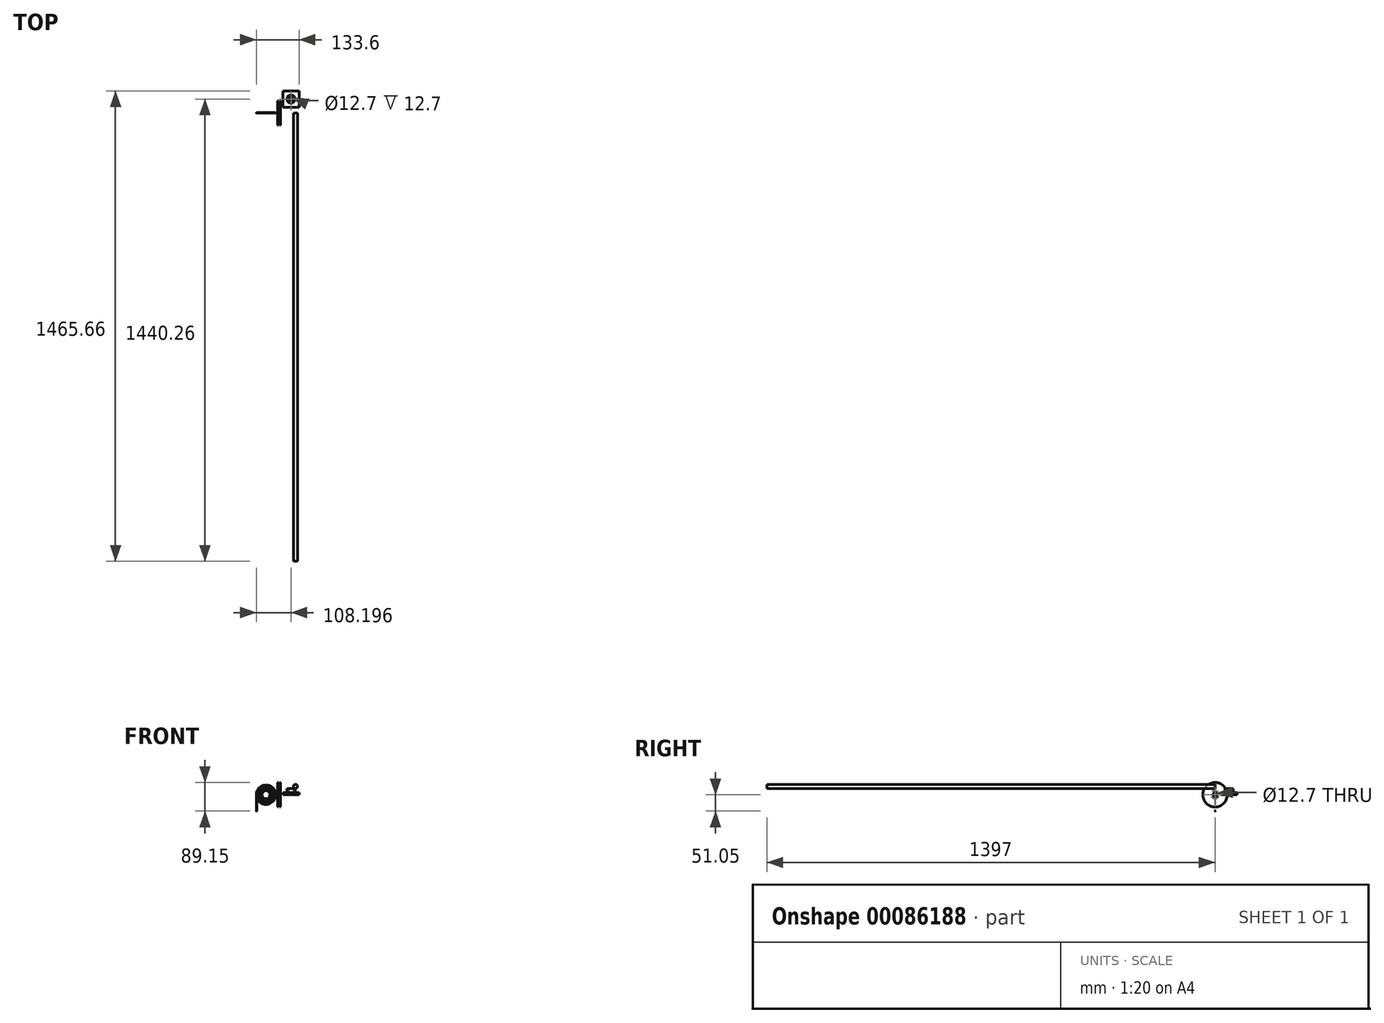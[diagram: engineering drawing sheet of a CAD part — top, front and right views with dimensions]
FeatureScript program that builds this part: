
annotation { "Feature Type Name" : "Feature", "Feature Type Description" : "" }
export const myFeature = defineFeature(function(context is Context, id is Id, definition is map)
    precondition{}
    {
        {
            var Q0;
            Q0=qCreatedBy(makeId("Front.planeOp"),FACE);
            var sketch = newSketch(context, id + "F0", { "sketchPlane" : qUnion([Q0])});
            skLineSegment(sketch, "E0", {"start": v(0, 0) * mm, "end": v(-68.9, 0) * mm, "construction": true});
            skLineSegment(sketch, "E1", {"start": v(0, 0) * mm, "end": v(0, 60.17) * mm, "construction": true});
            skLineSegment(sketch, "E2", {"start": v(-4.76, 6.35) * mm, "end": v(-4.76, 38.1) * mm});
            skLineSegment(sketch, "E3", {"start": v(-4.76, 38.1) * mm, "end": v(-1.59, 38.1) * mm});
            skLineSegment(sketch, "E4", {"start": v(-1.59, 38.1) * mm, "end": v(-1.59, 12.7) * mm});
            skLineSegment(sketch, "E5", {"start": v(-1.59, 12.7) * mm, "end": v(0, 12.7) * mm});
            skLineSegment(sketch, "E6", {"start": v(0, 12.7) * mm, "end": v(0, 6.35) * mm});
            skLineSegment(sketch, "E7", {"start": v(0, 6.35) * mm, "end": v(-4.76, 6.35) * mm});
            skLineSegment(sketch, "E8.MirrorCS", {"start": v(1.59, 12.7) * mm, "end": v(0, 12.7) * mm});
            skLineSegment(sketch, "E9.MirrorCS", {"start": v(1.59, 38.1) * mm, "end": v(1.59, 12.7) * mm});
            skLineSegment(sketch, "E10.MirrorCS", {"start": v(4.76, 38.1) * mm, "end": v(1.59, 38.1) * mm});
            skLineSegment(sketch, "E11.MirrorCS", {"start": v(4.76, 6.35) * mm, "end": v(4.76, 38.1) * mm});
            skLineSegment(sketch, "E12.MirrorCS", {"start": v(0, 6.35) * mm, "end": v(4.76, 6.35) * mm});
            skSolve(sketch);
        }
        {
            var Q0;
            Q0=makeQuery(id+"F0.imprint","IMPRINT",FACE,{"disambiguationData":[TD([[makeQuery(id+"F0.imprint","IMPRINT",EDGE,{"derivedFrom":sQuery(id+"F0.wireOp",EDGE,"E2")}),-1.0]])]});
            var Q1;
            Q1=makeQuery(id+"F0.imprint","IMPRINT",FACE,{"disambiguationData":[TD([[makeQuery(id+"F0.imprint","IMPRINT",EDGE,{"derivedFrom":sQuery(id+"F0.wireOp",EDGE,"E6")}),1.0]])]});
            var Q2;
            Q2=sQuery(id+"F0.wireOp",EDGE,"E0");
            revolve(context, id + "F1", {"entities" : qUnion([Q0, Q1]), "axis" : qUnion([Q2]), "revolveType" : RevolveType.FULL});
        }
        {
            var Q0;
            Q0=qCreatedBy(makeId("Front.planeOp"),FACE);
            var sketch = newSketch(context, id + "F2", { "sketchPlane" : qUnion([Q0])});
            skCircle(sketch, "E13", {"center": v(-40.88, 0) * mm, "radius": 12.7 * mm});
            skCircle(sketch, "E14", {"center": v(-40.88, 0) * mm, "radius": 14.29 * mm});
            skCircle(sketch, "E15", {"center": v(-40.88, 0) * mm, "radius": 15.88 * mm});
            skCircle(sketch, "E16", {"center": v(-40.88, 0) * mm, "radius": 17.46 * mm});
            skCircle(sketch, "E17", {"center": v(-40.88, 0) * mm, "radius": 19.05 * mm});
            skCircle(sketch, "E18", {"center": v(-40.88, 0) * mm, "radius": 20.64 * mm});
            skCircle(sketch, "E19", {"center": v(-40.88, 0) * mm, "radius": 22.22 * mm});
            skCircle(sketch, "E20", {"center": v(-40.88, 0) * mm, "radius": 23.81 * mm});
            skCircle(sketch, "E21", {"center": v(-40.88, 0) * mm, "radius": 25.4 * mm});
            skCircle(sketch, "E22", {"center": v(-40.88, 0) * mm, "radius": 26.99 * mm});
            skCircle(sketch, "E23", {"center": v(-40.88, 0) * mm, "radius": 28.57 * mm});
            skArc(sketch, "E24", {"start": v(-69.45, -9.66) * mm, "mid": v(-11.12, 4.9) * mm, "end": v(-71.04, 0) * mm});
            skLineSegment(sketch, "E25", {"start": v(-71.04, 0) * mm, "end": v(-71.04, -51.05) * mm});
            skLineSegment(sketch, "E26", {"start": v(-69.45, 0) * mm, "end": v(-69.45, -51.05) * mm});
            skLineSegment(sketch, "E27", {"start": v(-71.04, -51.05) * mm, "end": v(-69.45, -51.05) * mm});
            skSolve(sketch);
        }
        {
            var Q0;
            Q0=qCreatedBy(makeId("Top.planeOp"),FACE);
            var sketch = newSketch(context, id + "F3", { "sketchPlane" : qUnion([Q0])});
            skLineSegment(sketch, "E28.0", {"start": v(-10.72, 0) * mm, "end": v(-71.04, 0) * mm});
            skLineSegment(sketch, "E28.1", {"start": v(-12.3, 0) * mm, "end": v(-69.45, 0) * mm});
            skLineSegment(sketch, "E28.2", {"start": v(-13.9, 0) * mm, "end": v(-67.87, 0) * mm});
            skLineSegment(sketch, "E28.3", {"start": v(-15.48, 0) * mm, "end": v(-66.28, 0) * mm});
            skLineSegment(sketch, "E28.4", {"start": v(-17.07, 0) * mm, "end": v(-64.7, 0) * mm});
            skLineSegment(sketch, "E28.5", {"start": v(-18.65, 0) * mm, "end": v(-63.1, 0) * mm});
            skLineSegment(sketch, "E28.6", {"start": v(-20.24, 0) * mm, "end": v(-61.52, 0) * mm});
            skLineSegment(sketch, "E28.7", {"start": v(-21.83, 0) * mm, "end": v(-59.93, 0) * mm});
            skLineSegment(sketch, "E28.8", {"start": v(-23.42, 0) * mm, "end": v(-58.34, 0) * mm});
            skLineSegment(sketch, "E28.9", {"start": v(-25, 0) * mm, "end": v(-56.75, 0) * mm});
            skLineSegment(sketch, "E28.10", {"start": v(-26.6, 0) * mm, "end": v(-55.17, 0) * mm});
            skLineSegment(sketch, "E28.11", {"start": v(-28.18, 0) * mm, "end": v(-53.58, 0) * mm});
            skLineSegment(sketch, "E28.14", {"start": v(-71.04, 0) * mm, "end": v(-69.45, 0) * mm});
            skCircle(sketch, "E29", {"center": v(-11.5, 0) * mm, "radius": 0.8 * mm});
            skCircle(sketch, "E30", {"center": v(-13.1, 0) * mm, "radius": 0.8 * mm});
            skCircle(sketch, "E31", {"center": v(-14.68, 0) * mm, "radius": 0.8 * mm});
            skCircle(sketch, "E32", {"center": v(-16.27, 0) * mm, "radius": 0.8 * mm});
            skCircle(sketch, "E33", {"center": v(-17.86, 0) * mm, "radius": 0.8 * mm});
            skCircle(sketch, "E34", {"center": v(-19.45, 0) * mm, "radius": 0.8 * mm});
            skCircle(sketch, "E35", {"center": v(-21.03, 0) * mm, "radius": 0.8 * mm});
            skCircle(sketch, "E36", {"center": v(-22.62, 0) * mm, "radius": 0.8 * mm});
            skCircle(sketch, "E37", {"center": v(-24.2, 0) * mm, "radius": 0.8 * mm});
            skCircle(sketch, "E38", {"center": v(-25.8, 0) * mm, "radius": 0.8 * mm});
            skCircle(sketch, "E39", {"center": v(-27.38, 0) * mm, "radius": 0.8 * mm});
            skSolve(sketch);
        }
        {
            var Q0;
            {var subQ0=sQuery(id+"F3.wireOp",EDGE,"E28.0");Q0=makeQuery(id+"F3.imprint","IMPRINT",FACE,{"disambiguationData":[TD([[makeQuery(id+"F3.imprint","IMPRINT",EDGE,{"derivedFrom":subQ0}),-1.0]])]});}
            var Q1;
            {var subQ0=sQuery(id+"F3.wireOp",EDGE,"E30");var subQ1=sQuery(id+"F3.wireOp",EDGE,"E28.1");var subQ2=makeQuery(id+"F3.imprint","INTERSECT",VERTEX,{"derivedFrom":[sQuery(id+"F3.wireOp",EDGE,"E28.0"),subQ1,sQuery(id+"F3.wireOp",EDGE,"E29"),subQ0]});Q1=makeQuery(id+"F3.imprint","IMPRINT",FACE,{"disambiguationData":[TD([[makeQuery(id+"F3.imprint","IMPRINT",EDGE,{"disambiguationData":[TD([[subQ2,-1.0]])],"derivedFrom":subQ1}),-1.0]])]});}
            var Q2;
            {var subQ0=sQuery(id+"F3.wireOp",EDGE,"E31");var subQ1=sQuery(id+"F3.wireOp",EDGE,"E28.2");var subQ2=makeQuery(id+"F3.imprint","INTERSECT",VERTEX,{"derivedFrom":[sQuery(id+"F3.wireOp",EDGE,"E28.1"),subQ1,sQuery(id+"F3.wireOp",EDGE,"E30"),subQ0]});Q2=makeQuery(id+"F3.imprint","IMPRINT",FACE,{"disambiguationData":[TD([[makeQuery(id+"F3.imprint","IMPRINT",EDGE,{"disambiguationData":[TD([[subQ2,-1.0]])],"derivedFrom":subQ1}),-1.0]])]});}
            var Q3;
            {var subQ0=sQuery(id+"F3.wireOp",EDGE,"E32");var subQ1=sQuery(id+"F3.wireOp",EDGE,"E28.3");var subQ2=makeQuery(id+"F3.imprint","INTERSECT",VERTEX,{"derivedFrom":[sQuery(id+"F3.wireOp",EDGE,"E28.2"),subQ1,sQuery(id+"F3.wireOp",EDGE,"E31"),subQ0]});Q3=makeQuery(id+"F3.imprint","IMPRINT",FACE,{"disambiguationData":[TD([[makeQuery(id+"F3.imprint","IMPRINT",EDGE,{"disambiguationData":[TD([[subQ2,-1.0]])],"derivedFrom":subQ1}),-1.0]])]});}
            var Q4;
            {var subQ0=sQuery(id+"F3.wireOp",EDGE,"E33");var subQ1=sQuery(id+"F3.wireOp",EDGE,"E28.4");var subQ2=makeQuery(id+"F3.imprint","INTERSECT",VERTEX,{"derivedFrom":[sQuery(id+"F3.wireOp",EDGE,"E28.3"),subQ1,sQuery(id+"F3.wireOp",EDGE,"E32"),subQ0]});Q4=makeQuery(id+"F3.imprint","IMPRINT",FACE,{"disambiguationData":[TD([[makeQuery(id+"F3.imprint","IMPRINT",EDGE,{"disambiguationData":[TD([[subQ2,-1.0]])],"derivedFrom":subQ1}),-1.0]])]});}
            var Q5;
            {var subQ0=sQuery(id+"F3.wireOp",EDGE,"E34");var subQ1=sQuery(id+"F3.wireOp",EDGE,"E28.5");var subQ2=makeQuery(id+"F3.imprint","INTERSECT",VERTEX,{"derivedFrom":[sQuery(id+"F3.wireOp",EDGE,"E28.4"),subQ1,sQuery(id+"F3.wireOp",EDGE,"E33"),subQ0]});Q5=makeQuery(id+"F3.imprint","IMPRINT",FACE,{"disambiguationData":[TD([[makeQuery(id+"F3.imprint","IMPRINT",EDGE,{"disambiguationData":[TD([[subQ2,-1.0]])],"derivedFrom":subQ1}),-1.0]])]});}
            var Q6;
            {var subQ0=sQuery(id+"F3.wireOp",EDGE,"E35");var subQ1=sQuery(id+"F3.wireOp",EDGE,"E28.6");var subQ2=makeQuery(id+"F3.imprint","INTERSECT",VERTEX,{"derivedFrom":[sQuery(id+"F3.wireOp",EDGE,"E28.5"),subQ1,sQuery(id+"F3.wireOp",EDGE,"E34"),subQ0]});Q6=makeQuery(id+"F3.imprint","IMPRINT",FACE,{"disambiguationData":[TD([[makeQuery(id+"F3.imprint","IMPRINT",EDGE,{"disambiguationData":[TD([[subQ2,-1.0]])],"derivedFrom":subQ1}),-1.0]])]});}
            var Q7;
            {var subQ0=sQuery(id+"F3.wireOp",EDGE,"E36");var subQ1=sQuery(id+"F3.wireOp",EDGE,"E28.7");var subQ2=makeQuery(id+"F3.imprint","INTERSECT",VERTEX,{"derivedFrom":[sQuery(id+"F3.wireOp",EDGE,"E28.6"),subQ1,sQuery(id+"F3.wireOp",EDGE,"E35"),subQ0]});Q7=makeQuery(id+"F3.imprint","IMPRINT",FACE,{"disambiguationData":[TD([[makeQuery(id+"F3.imprint","IMPRINT",EDGE,{"disambiguationData":[TD([[subQ2,-1.0]])],"derivedFrom":subQ1}),-1.0]])]});}
            var Q8;
            {var subQ0=sQuery(id+"F3.wireOp",EDGE,"E37");var subQ1=sQuery(id+"F3.wireOp",EDGE,"E28.8");var subQ2=makeQuery(id+"F3.imprint","INTERSECT",VERTEX,{"derivedFrom":[sQuery(id+"F3.wireOp",EDGE,"E28.7"),subQ1,sQuery(id+"F3.wireOp",EDGE,"E36"),subQ0]});Q8=makeQuery(id+"F3.imprint","IMPRINT",FACE,{"disambiguationData":[TD([[makeQuery(id+"F3.imprint","IMPRINT",EDGE,{"disambiguationData":[TD([[subQ2,-1.0]])],"derivedFrom":subQ1}),-1.0]])]});}
            var Q9;
            {var subQ0=sQuery(id+"F3.wireOp",EDGE,"E38");var subQ1=sQuery(id+"F3.wireOp",EDGE,"E28.9");var subQ2=makeQuery(id+"F3.imprint","INTERSECT",VERTEX,{"derivedFrom":[sQuery(id+"F3.wireOp",EDGE,"E28.8"),subQ1,sQuery(id+"F3.wireOp",EDGE,"E37"),subQ0]});Q9=makeQuery(id+"F3.imprint","IMPRINT",FACE,{"disambiguationData":[TD([[makeQuery(id+"F3.imprint","IMPRINT",EDGE,{"disambiguationData":[TD([[subQ2,-1.0]])],"derivedFrom":subQ1}),-1.0]])]});}
            var Q10;
            {var subQ0=sQuery(id+"F3.wireOp",EDGE,"E39");var subQ1=sQuery(id+"F3.wireOp",EDGE,"E28.10");var subQ3=makeQuery(id+"F3.imprint","INTERSECT",VERTEX,{"derivedFrom":[subQ1,subQ0]});Q10=makeQuery(id+"F3.imprint","IMPRINT",FACE,{"disambiguationData":[TD([[makeQuery(id+"F3.imprint","IMPRINT",EDGE,{"disambiguationData":[TD([[subQ3,1.0]])],"derivedFrom":subQ1}),-1.0]])]});}
            var Q11;
            {var subQ0=sQuery(id+"F3.wireOp",EDGE,"E28.0");Q11=makeQuery(id+"F3.imprint","IMPRINT",FACE,{"disambiguationData":[TD([[makeQuery(id+"F3.imprint","IMPRINT",EDGE,{"derivedFrom":subQ0}),1.0]])]});}
            var Q12;
            {var subQ0=sQuery(id+"F3.wireOp",EDGE,"E30");var subQ1=sQuery(id+"F3.wireOp",EDGE,"E28.1");var subQ2=makeQuery(id+"F3.imprint","INTERSECT",VERTEX,{"derivedFrom":[sQuery(id+"F3.wireOp",EDGE,"E28.0"),subQ1,sQuery(id+"F3.wireOp",EDGE,"E29"),subQ0]});Q12=makeQuery(id+"F3.imprint","IMPRINT",FACE,{"disambiguationData":[TD([[makeQuery(id+"F3.imprint","IMPRINT",EDGE,{"disambiguationData":[TD([[subQ2,-1.0]])],"derivedFrom":subQ1}),1.0]])]});}
            var Q13;
            {var subQ0=sQuery(id+"F3.wireOp",EDGE,"E31");var subQ1=sQuery(id+"F3.wireOp",EDGE,"E28.2");var subQ2=makeQuery(id+"F3.imprint","INTERSECT",VERTEX,{"derivedFrom":[sQuery(id+"F3.wireOp",EDGE,"E28.1"),subQ1,sQuery(id+"F3.wireOp",EDGE,"E30"),subQ0]});Q13=makeQuery(id+"F3.imprint","IMPRINT",FACE,{"disambiguationData":[TD([[makeQuery(id+"F3.imprint","IMPRINT",EDGE,{"disambiguationData":[TD([[subQ2,-1.0]])],"derivedFrom":subQ1}),1.0]])]});}
            var Q14;
            {var subQ0=sQuery(id+"F3.wireOp",EDGE,"E32");var subQ1=sQuery(id+"F3.wireOp",EDGE,"E28.3");var subQ2=makeQuery(id+"F3.imprint","INTERSECT",VERTEX,{"derivedFrom":[sQuery(id+"F3.wireOp",EDGE,"E28.2"),subQ1,sQuery(id+"F3.wireOp",EDGE,"E31"),subQ0]});Q14=makeQuery(id+"F3.imprint","IMPRINT",FACE,{"disambiguationData":[TD([[makeQuery(id+"F3.imprint","IMPRINT",EDGE,{"disambiguationData":[TD([[subQ2,-1.0]])],"derivedFrom":subQ1}),1.0]])]});}
            var Q15;
            {var subQ0=sQuery(id+"F3.wireOp",EDGE,"E33");var subQ1=sQuery(id+"F3.wireOp",EDGE,"E28.4");var subQ2=makeQuery(id+"F3.imprint","INTERSECT",VERTEX,{"derivedFrom":[sQuery(id+"F3.wireOp",EDGE,"E28.3"),subQ1,sQuery(id+"F3.wireOp",EDGE,"E32"),subQ0]});Q15=makeQuery(id+"F3.imprint","IMPRINT",FACE,{"disambiguationData":[TD([[makeQuery(id+"F3.imprint","IMPRINT",EDGE,{"disambiguationData":[TD([[subQ2,-1.0]])],"derivedFrom":subQ1}),1.0]])]});}
            var Q16;
            {var subQ0=sQuery(id+"F3.wireOp",EDGE,"E34");var subQ1=sQuery(id+"F3.wireOp",EDGE,"E28.5");var subQ2=makeQuery(id+"F3.imprint","INTERSECT",VERTEX,{"derivedFrom":[sQuery(id+"F3.wireOp",EDGE,"E28.4"),subQ1,sQuery(id+"F3.wireOp",EDGE,"E33"),subQ0]});Q16=makeQuery(id+"F3.imprint","IMPRINT",FACE,{"disambiguationData":[TD([[makeQuery(id+"F3.imprint","IMPRINT",EDGE,{"disambiguationData":[TD([[subQ2,-1.0]])],"derivedFrom":subQ1}),1.0]])]});}
            var Q17;
            {var subQ0=sQuery(id+"F3.wireOp",EDGE,"E35");var subQ1=sQuery(id+"F3.wireOp",EDGE,"E28.6");var subQ2=makeQuery(id+"F3.imprint","INTERSECT",VERTEX,{"derivedFrom":[sQuery(id+"F3.wireOp",EDGE,"E28.5"),subQ1,sQuery(id+"F3.wireOp",EDGE,"E34"),subQ0]});Q17=makeQuery(id+"F3.imprint","IMPRINT",FACE,{"disambiguationData":[TD([[makeQuery(id+"F3.imprint","IMPRINT",EDGE,{"disambiguationData":[TD([[subQ2,-1.0]])],"derivedFrom":subQ1}),1.0]])]});}
            var Q18;
            {var subQ0=sQuery(id+"F3.wireOp",EDGE,"E36");var subQ1=sQuery(id+"F3.wireOp",EDGE,"E28.7");var subQ2=makeQuery(id+"F3.imprint","INTERSECT",VERTEX,{"derivedFrom":[sQuery(id+"F3.wireOp",EDGE,"E28.6"),subQ1,sQuery(id+"F3.wireOp",EDGE,"E35"),subQ0]});Q18=makeQuery(id+"F3.imprint","IMPRINT",FACE,{"disambiguationData":[TD([[makeQuery(id+"F3.imprint","IMPRINT",EDGE,{"disambiguationData":[TD([[subQ2,-1.0]])],"derivedFrom":subQ1}),1.0]])]});}
            var Q19;
            {var subQ0=sQuery(id+"F3.wireOp",EDGE,"E37");var subQ1=sQuery(id+"F3.wireOp",EDGE,"E28.8");var subQ2=makeQuery(id+"F3.imprint","INTERSECT",VERTEX,{"derivedFrom":[sQuery(id+"F3.wireOp",EDGE,"E28.7"),subQ1,sQuery(id+"F3.wireOp",EDGE,"E36"),subQ0]});Q19=makeQuery(id+"F3.imprint","IMPRINT",FACE,{"disambiguationData":[TD([[makeQuery(id+"F3.imprint","IMPRINT",EDGE,{"disambiguationData":[TD([[subQ2,-1.0]])],"derivedFrom":subQ1}),1.0]])]});}
            var Q20;
            {var subQ0=sQuery(id+"F3.wireOp",EDGE,"E38");var subQ1=sQuery(id+"F3.wireOp",EDGE,"E28.9");var subQ2=makeQuery(id+"F3.imprint","INTERSECT",VERTEX,{"derivedFrom":[sQuery(id+"F3.wireOp",EDGE,"E28.8"),subQ1,sQuery(id+"F3.wireOp",EDGE,"E37"),subQ0]});Q20=makeQuery(id+"F3.imprint","IMPRINT",FACE,{"disambiguationData":[TD([[makeQuery(id+"F3.imprint","IMPRINT",EDGE,{"disambiguationData":[TD([[subQ2,-1.0]])],"derivedFrom":subQ1}),1.0]])]});}
            var Q21;
            {var subQ0=sQuery(id+"F3.wireOp",EDGE,"E39");var subQ1=sQuery(id+"F3.wireOp",EDGE,"E28.10");var subQ3=makeQuery(id+"F3.imprint","INTERSECT",VERTEX,{"derivedFrom":[subQ1,subQ0]});Q21=makeQuery(id+"F3.imprint","IMPRINT",FACE,{"disambiguationData":[TD([[makeQuery(id+"F3.imprint","IMPRINT",EDGE,{"disambiguationData":[TD([[subQ3,1.0]])],"derivedFrom":subQ1}),1.0]])]});}
            var Q22;
            Q22=sQuery(id+"F2.wireOp",EDGE,"E13");
            sweep(context, id + "F4", {"profiles" : qUnion([Q0, Q1, Q2, Q3, Q4, Q5, Q6, Q7, Q8, Q9, Q10, Q11, Q12, Q13, Q14, Q15, Q16, Q17, Q18, Q19, Q20, Q21]), "path" : qUnion([Q22])});
        }
        {
            var Q0;
            Q0=qCreatedBy(makeId("Top.planeOp"),FACE);
            var sketch = newSketch(context, id + "F5", { "sketchPlane" : qUnion([Q0])});
            skCircle(sketch, "E40", {"center": v(-70.25, 0) * mm, "radius": 0.8 * mm});
            skSolve(sketch);
        }
        {
            var Q0;
            Q0 = qSketchRegion(id + "F5", true);
            var Q1;
            Q1=sQuery(id+"F2.wireOp",EDGE,"E26");
            sweep(context, id + "F6", {"operationType" : NewBodyOperationType.ADD, "profiles" : qUnion([Q0]), "path" : qUnion([Q1])});
        }
        {
            var Q0;
            Q0=qCreatedBy(makeId("Front.planeOp"),FACE);
            var sketch = newSketch(context, id + "F7", { "sketchPlane" : qUnion([Q0])});
            skCircle(sketch, "E41", {"center": v(51.02, 26.07) * mm, "radius": 6.35 * mm});
            skSolve(sketch);
        }
        {
            var Q0;
            Q0=makeQuery(id+"F7.imprint","IMPRINT",FACE,{"disambiguationData":[TD([[makeQuery(id+"F7.imprint","IMPRINT",EDGE,{"derivedFrom":sQuery(id+"F7.wireOp",EDGE,"E41")}),1.0]])]});
            extrude(context, id + "F8", {"entities" : qUnion([Q0]), "depth" : 1397 * mm});
        }
        {
            var Q0;
            Q0=qCreatedBy(makeId("Top.planeOp"),FACE);
            var sketch = newSketch(context, id + "F9", { "sketchPlane" : qUnion([Q0])});
            skLineSegment(sketch, "E42.bottom", {"start": v(62.56, 68.66) * mm, "end": v(11.76, 68.66) * mm});
            skLineSegment(sketch, "E42.top", {"start": v(62.56, 17.86) * mm, "end": v(11.76, 17.86) * mm});
            skLineSegment(sketch, "E42.left", {"start": v(62.56, 68.66) * mm, "end": v(62.56, 17.86) * mm});
            skLineSegment(sketch, "E42.right", {"start": v(11.76, 68.66) * mm, "end": v(11.76, 17.86) * mm});
            skSolve(sketch);
        }
        {
            var Q0;
            Q0=makeQuery(id+"F9.imprint","IMPRINT",FACE,{"disambiguationData":[TD([[makeQuery(id+"F9.imprint","IMPRINT",EDGE,{"derivedFrom":sQuery(id+"F9.wireOp",EDGE,"E42.bottom")}),1.0]])]});
            extrude(context, id + "F10", {"entities" : qUnion([Q0]), "depth" : 6.35 * mm});
        }
        {
            var Q0;
            Q0=makeQuery(id+"F10.opExtrude","CAP_FACE",FACE,{"disambiguationData":[OSD([sQuery(id+"F9.wireOp",EDGE,"E42.bottom"),sQuery(id+"F9.wireOp",EDGE,"E42.top"),sQuery(id+"F9.wireOp",EDGE,"E42.left"),sQuery(id+"F9.wireOp",EDGE,"E42.right")])],"isStart":false});
            var sketch = newSketch(context, id + "F11", { "sketchPlane" : qUnion([Q0])});
            skLineSegment(sketch, "E43.0", {"start": v(62.56, 17.86) * mm, "end": v(11.76, 17.86) * mm});
            skLineSegment(sketch, "E43.1", {"start": v(62.56, 68.66) * mm, "end": v(62.56, 17.86) * mm});
            skLineSegment(sketch, "E43.2", {"start": v(11.76, 68.66) * mm, "end": v(11.76, 17.86) * mm});
            skLineSegment(sketch, "E43.3", {"start": v(62.56, 68.66) * mm, "end": v(11.76, 68.66) * mm});
            skLineSegment(sketch, "E44", {"start": v(11.76, 17.86) * mm, "end": v(62.56, 68.66) * mm, "construction": true});
            skCircle(sketch, "E45", {"center": v(37.16, 43.26) * mm, "radius": 6.35 * mm});
            skCircle(sketch, "E46", {"center": v(37.16, 43.26) * mm, "radius": 12.7 * mm});
            skSolve(sketch);
        }
        {
            var Q0;
            Q0=makeQuery(id+"F11.imprint","IMPRINT",FACE,{"disambiguationData":[TD([[makeQuery(id+"F11.imprint","IMPRINT",EDGE,{"derivedFrom":sQuery(id+"F11.wireOp",EDGE,"E45")}),-1.0]])]});
            extrude(context, id + "F12", {"entities" : qUnion([Q0]), "operationType" : NewBodyOperationType.ADD, "depth" : 12.7 * mm});
        }
    });
